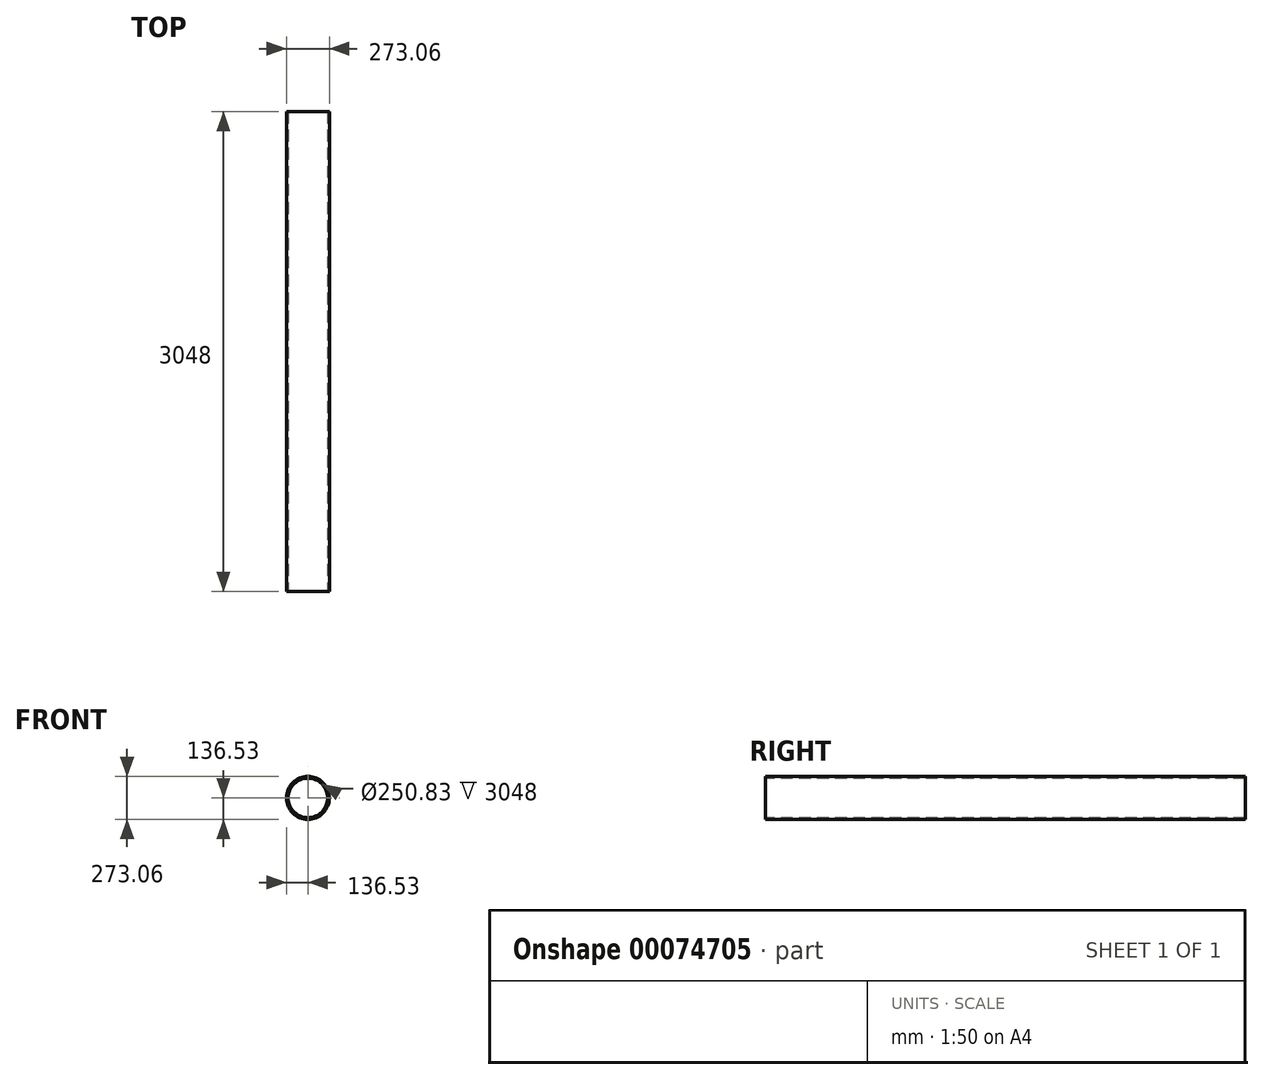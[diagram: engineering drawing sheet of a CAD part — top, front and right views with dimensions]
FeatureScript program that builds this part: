
annotation { "Feature Type Name" : "Feature", "Feature Type Description" : "" }
export const myFeature = defineFeature(function(context is Context, id is Id, definition is map)
    precondition{}
    {
        {
            var Q0;
            Q0=qCreatedBy(makeId("Front.planeOp"),FACE);
            var sketch = newSketch(context, id + "F0", { "sketchPlane" : qUnion([Q0])});
            skCircle(sketch, "E0", {"center": v(0, 0) * mm, "radius": 136.53 * mm});
            skCircle(sketch, "E1", {"center": v(0, 0) * mm, "radius": 125.41 * mm});
            skCircle(sketch, "E2", {"center": v(0, -20) * mm, "radius": 1.87 * mm});
            skSolve(sketch);
        }
        {
            var Q0;
            Q0 = qSketchRegion(id + "F0", true);
            extrude(context, id + "F1", {"entities" : qUnion([Q0]), "oppositeDirection" : true, "depth" : 3048 * mm});
        }
    });
